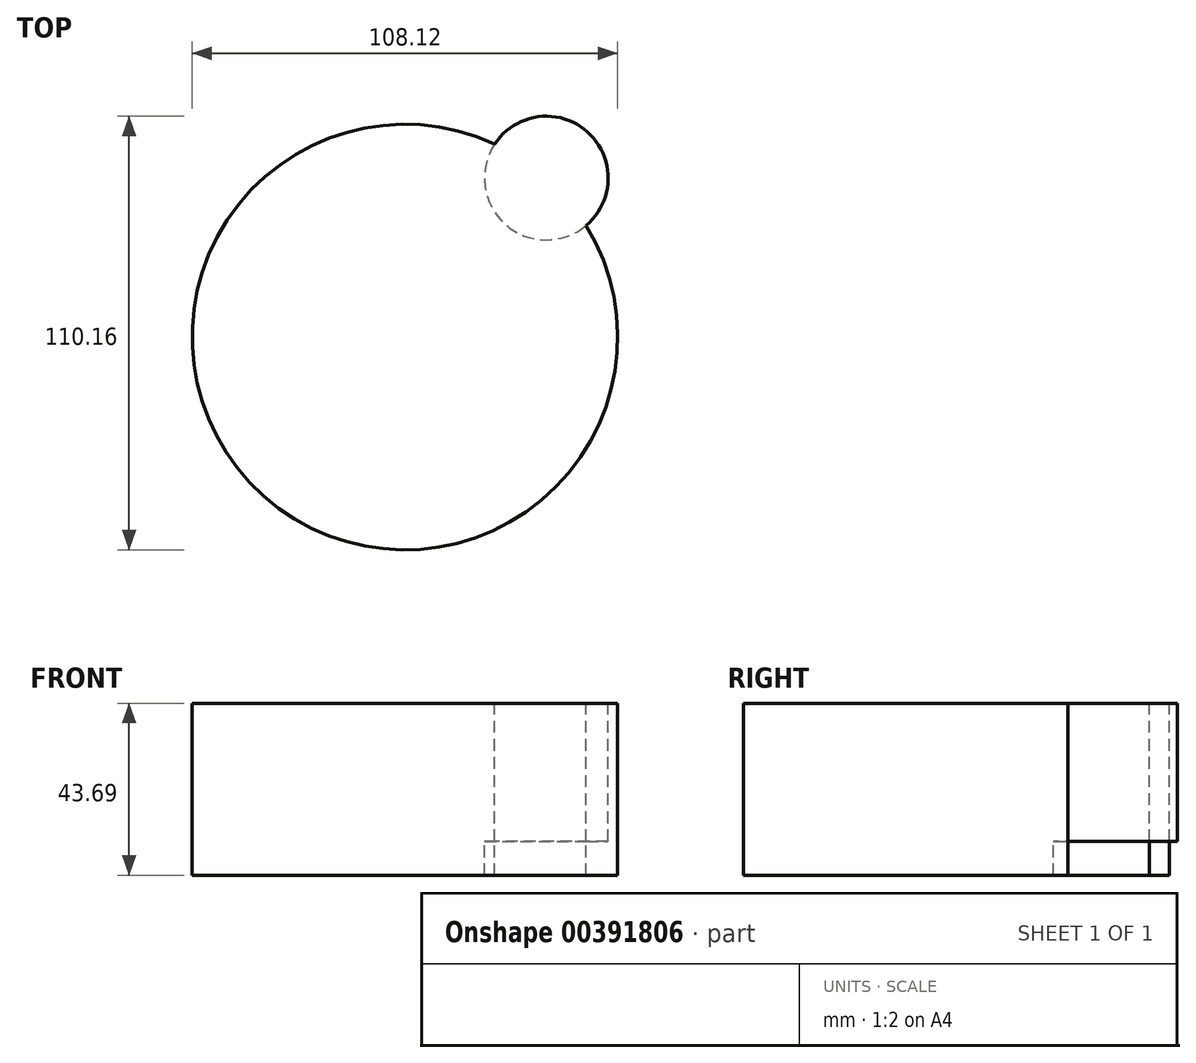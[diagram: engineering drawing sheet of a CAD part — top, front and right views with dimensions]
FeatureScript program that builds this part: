
annotation { "Feature Type Name" : "Feature", "Feature Type Description" : "" }
export const myFeature = defineFeature(function(context is Context, id is Id, definition is map)
    precondition{}
    {
        {
            var Q0;
            Q0=qCreatedBy(makeId("Top.planeOp"),FACE);
            var sketch = newSketch(context, id + "F0", { "sketchPlane" : qUnion([Q0])});
            skCircle(sketch, "E0", {"center": v(0, 0) * mm, "radius": 54.06 * mm});
            skCircle(sketch, "E1", {"center": v(35.93, 40.4) * mm, "radius": 15.7 * mm});
            skPoint(sketch, "E2", {"position": v(51.63, 40.4) * mm});
            skSolve(sketch);
        }
        {
            var Q0;
            {var subQ0=sQuery(id+"F0.wireOp",EDGE,"E1");var subQ1=sQuery(id+"F0.wireOp",EDGE,"E0");var subQ2=makeQuery(id+"F0.imprint","INTERSECT",VERTEX,{"disambiguationData":[OD(0.0)],"derivedFrom":[subQ1,subQ0]});Q0=makeQuery(id+"F0.imprint","IMPRINT",FACE,{"disambiguationData":[TD([[makeQuery(id+"F0.imprint","IMPRINT",EDGE,{"disambiguationData":[TD([[subQ2,-1.0]])],"derivedFrom":subQ1}),1.0]])]});}
            extrude(context, id + "F1", {"entities" : qUnion([Q0]), "oppositeDirection" : true, "depth" : 43.69 * mm});
        }
        {
            var Q0;
            Q0 = qSketchRegion(id + "F0", true);
            extrude(context, id + "F2", {"entities" : qUnion([Q0]), "operationType" : NewBodyOperationType.ADD, "oppositeDirection" : true, "depth" : 35.05 * mm});
        }
    });
